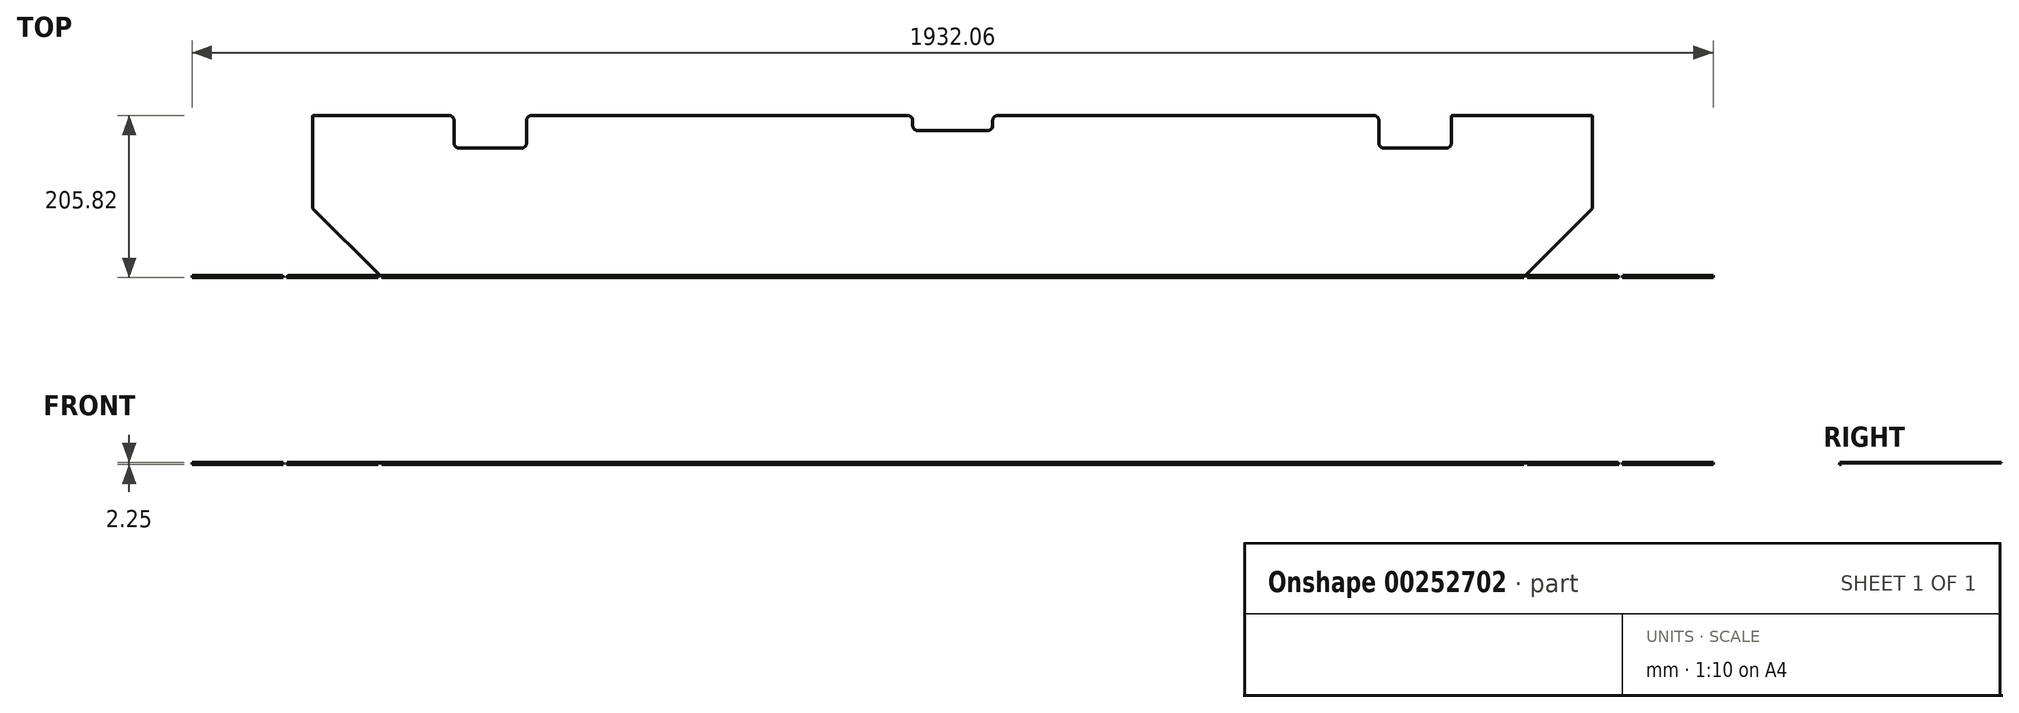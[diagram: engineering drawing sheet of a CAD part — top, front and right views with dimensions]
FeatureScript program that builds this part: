
annotation { "Feature Type Name" : "Feature", "Feature Type Description" : "" }
export const myFeature = defineFeature(function(context is Context, id is Id, definition is map)
    precondition{}
    {
        {
            assignVariable(context, id + "F0", {"name" : "Thickness", "anyValue" : .4});
        }
        {
            assignVariable(context, id + "F1", {"name" : "Height", "anyValue" : 2.25});
        }
        {
            var Q0;
            Q0=qCreatedBy(makeId("Top.planeOp"),FACE);
            var sketch = newSketch(context, id + "F2", { "sketchPlane" : qUnion([Q0])});
            skLineSegment(sketch, "E0.bottom", {"start": v(-812.8, 0) * mm, "end": v(812.8, 0) * mm});
            skLineSegment(sketch, "E0.top", {"start": v(-727.49, -203.2) * mm, "end": v(727.49, -203.2) * mm});
            skLineSegment(sketch, "E0.left", {"start": v(-812.8, 0) * mm, "end": v(-812.8, -117.89) * mm});
            skLineSegment(sketch, "E0.right", {"start": v(812.8, 0) * mm, "end": v(812.8, -117.89) * mm});
            skLineSegment(sketch, "E1", {"start": v(0, 0) * mm, "end": v(0, -68.91) * mm, "construction": true});
            skLineSegment(sketch, "E2", {"start": v(-812.8, -117.89) * mm, "end": v(-727.49, -203.2) * mm});
            skLineSegment(sketch, "E3", {"start": v(727.49, -203.2) * mm, "end": v(812.8, -117.89) * mm});
            skSolve(sketch);
        }
        {
            var Q0;
            Q0=qSketchRegion(id+"F2",true);
            extrude(context, id + "F3", {"entities" : qUnion([Q0]), "oppositeDirection" : true, "depth" : (getVariable(context, 'Thickness')) * mm});
        }
        {
            var Q0;
            Q0=makeQuery(id+"F3.opExtrude","CAP_FACE",FACE,{"disambiguationData":[OSD([sQuery(id+"F2.wireOp",EDGE,"E0.bottom"),sQuery(id+"F2.wireOp",EDGE,"E0.top"),sQuery(id+"F2.wireOp",EDGE,"E0.left"),sQuery(id+"F2.wireOp",EDGE,"E0.right"),sQuery(id+"F2.wireOp",EDGE,"E2"),sQuery(id+"F2.wireOp",EDGE,"E3")])],"isStart":true});
            var sketch = newSketch(context, id + "F4", { "sketchPlane" : qUnion([Q0])});
            skLineSegment(sketch, "E4.bottom", {"start": v(-1016, -203.2) * mm, "end": v(1016, -203.2) * mm});
            skLineSegment(sketch, "E4.top", {"start": v(-1016, -211.14) * mm, "end": v(1016, -211.14) * mm});
            skLineSegment(sketch, "E4.left", {"start": v(-1016, -203.2) * mm, "end": v(-1016, -211.14) * mm});
            skLineSegment(sketch, "E4.right", {"start": v(1016, -203.2) * mm, "end": v(1016, -211.14) * mm});
            skSolve(sketch);
        }
        {
            var Q0;
            Q0=qSketchRegion(id+"F4",true);
            extrude(context, id + "F5", {"entities" : qUnion([Q0]), "oppositeDirection" : true, "depth" : (getVariable(context, 'Height')) * mm});
        }
        {
            var Q0;
            Q0=qCreatedBy(makeId("Right.planeOp"),FACE);
            var sketch = newSketch(context, id + "F6", { "sketchPlane" : qUnion([Q0])});
            skLineSegment(sketch, "E5", {"start": v(-209.64, -12.7) * mm, "end": v(-211.14, -12.7) * mm});
            skLineSegment(sketch, "E6", {"start": v(-211.14, -12.7) * mm, "end": v(-211.14, 0) * mm});
            skLineSegment(sketch, "E7", {"start": v(-211.14, 0) * mm, "end": v(-204.7, 0) * mm});
            skFitSpline(sketch, "E8", {"points": [v(-204.7, 0) * mm, v(-204.89, -0.82) * mm, v(-207.45, -4.89) * mm, v(-209.64, -12.7) * mm], "startDerivative": vector(0, -4.3) * mm, "endDerivative": vector(-0.41, -10.99) * mm});
            skSolve(sketch);
        }
        {
            var Q0;
            Q0=qSketchRegion(id+"F6",true);
            extrude(context, id + "F7", {"entities" : qUnion([Q0]), "operationType" : NewBodyOperationType.REMOVE, "endBound" : BoundingType.THROUGH_ALL, "oppositeDirection" : true, "depth" : 25.4 * mm, "hasSecondDirection" : true, "secondDirectionBound" : SecondDirectionBoundingType.THROUGH_ALL, "secondDirectionOppositeDirection" : false, "secondDirectionDepth" : 25.4 * mm});
        }
        {
            var Q0;
            Q0=makeQuery(id+"F5.opExtrude","SWEPT_FACE",FACE,{"disambiguationData":[OSD([sQuery(id+"F4.wireOp",EDGE,"E4.right")])]});
            var sketch = newSketch(context, id + "F8", { "sketchPlane" : qUnion([Q0])});
            skLineSegment(sketch, "E9", {"start": v(-211.14, -31.75) * mm, "end": v(-211.14, -57.15) * mm});
            skLineSegment(sketch, "E10", {"start": v(-211.14, -57.15) * mm, "end": v(-203.2, -57.15) * mm});
            skLineSegment(sketch, "E11", {"start": v(-203.2, -57.15) * mm, "end": v(-203.2, -23.81) * mm});
            skLineSegment(sketch, "E12", {"start": v(-203.2, -23.81) * mm, "end": v(-211.14, -31.75) * mm});
            skSolve(sketch);
        }
        {
            var Q0;
            Q0 = qSketchRegion(id + "F8", true);
            extrude(context, id + "F9", {"entities" : qUnion([Q0]), "operationType" : NewBodyOperationType.REMOVE, "endBound" : BoundingType.THROUGH_ALL, "oppositeDirection" : true, "depth" : 25.4 * mm});
        }
        {
            var Q0;
            Q0=makeQuery(id+"F5.opExtrude","CAP_FACE",FACE,{"disambiguationData":[OSD([sQuery(id+"F4.wireOp",EDGE,"E4.bottom"),sQuery(id+"F4.wireOp",EDGE,"E4.top"),sQuery(id+"F4.wireOp",EDGE,"E4.left"),sQuery(id+"F4.wireOp",EDGE,"E4.right")])],"isStart":true});
            var sketch = newSketch(context, id + "F10", { "sketchPlane" : qUnion([Q0])});
            skLineSegment(sketch, "E13", {"start": v(-724.2, -203.2) * mm, "end": v(-727.49, -211.14) * mm});
            skLineSegment(sketch, "E14", {"start": v(-727.49, -211.14) * mm, "end": v(-730.78, -203.2) * mm});
            skLineSegment(sketch, "E15", {"start": v(-730.78, -203.2) * mm, "end": v(-724.2, -203.2) * mm});
            skLineSegment(sketch, "E16", {"start": v(-727.49, -211.14) * mm, "end": v(-727.49, -203.2) * mm, "construction": true});
            skPoint(sketch, "E16.endSnap0", {"position": v(-727.49, -203.2) * mm});
            skLineSegment(sketch, "E17", {"start": v(-844.85, -203.2) * mm, "end": v(-848.14, -211.14) * mm});
            skLineSegment(sketch, "E18", {"start": v(-848.14, -211.14) * mm, "end": v(-851.43, -203.2) * mm});
            skLineSegment(sketch, "E19", {"start": v(-851.43, -203.2) * mm, "end": v(-844.85, -203.2) * mm});
            skLineSegment(sketch, "E20", {"start": v(-848.14, -211.14) * mm, "end": v(-848.14, -203.2) * mm, "construction": true});
            skPoint(sketch, "E20.endSnap0", {"position": v(-848.14, -203.2) * mm});
            skLineSegment(sketch, "E21", {"start": v(0, 0) * mm, "end": v(0, -289.87) * mm, "construction": true});
            skLineSegment(sketch, "E22.MirrorCS", {"start": v(724.2, -203.2) * mm, "end": v(727.49, -211.14) * mm});
            skLineSegment(sketch, "E23.MirrorCS", {"start": v(727.49, -211.14) * mm, "end": v(730.78, -203.2) * mm});
            skLineSegment(sketch, "E24.MirrorCS", {"start": v(727.49, -211.14) * mm, "end": v(727.49, -203.2) * mm, "construction": true});
            skLineSegment(sketch, "E25.MirrorCS", {"start": v(730.78, -203.2) * mm, "end": v(724.2, -203.2) * mm});
            skLineSegment(sketch, "E26.MirrorCS", {"start": v(844.85, -203.2) * mm, "end": v(848.14, -211.14) * mm});
            skLineSegment(sketch, "E27.MirrorCS", {"start": v(848.14, -211.14) * mm, "end": v(851.43, -203.2) * mm});
            skLineSegment(sketch, "E28.MirrorCS", {"start": v(851.43, -203.2) * mm, "end": v(844.85, -203.2) * mm});
            skLineSegment(sketch, "E29.MirrorCS", {"start": v(848.14, -211.14) * mm, "end": v(848.14, -203.2) * mm, "construction": true});
            skPoint(sketch, "E30.MirrorP", {"position": v(727.49, -203.2) * mm});
            skPoint(sketch, "E31.MirrorP", {"position": v(848.14, -203.2) * mm});
            skLineSegment(sketch, "E32.bottom", {"start": v(-1016, -203.2) * mm, "end": v(-966.03, -203.2) * mm});
            skLineSegment(sketch, "E32.top", {"start": v(-1016, -211.14) * mm, "end": v(-966.03, -211.14) * mm});
            skLineSegment(sketch, "E32.left", {"start": v(-1016, -203.2) * mm, "end": v(-1016, -211.14) * mm});
            skLineSegment(sketch, "E32.right", {"start": v(-966.03, -203.2) * mm, "end": v(-966.03, -211.14) * mm});
            skLineSegment(sketch, "E33.MirrorCS", {"start": v(1016, -203.2) * mm, "end": v(1016, -211.14) * mm});
            skLineSegment(sketch, "E34.MirrorCS", {"start": v(966.03, -203.2) * mm, "end": v(966.03, -211.14) * mm});
            skLineSegment(sketch, "E35.MirrorCS", {"start": v(1016, -211.14) * mm, "end": v(966.03, -211.14) * mm});
            skLineSegment(sketch, "E36.MirrorCS", {"start": v(1016, -203.2) * mm, "end": v(966.03, -203.2) * mm});
            skLineSegment(sketch, "E37.0", {"start": v(-812.8, -117.89) * mm, "end": v(-727.49, -203.2) * mm, "construction": true});
            skLineSegment(sketch, "E38", {"start": v(-848.14, -211.14) * mm, "end": v(-727.49, -211.14) * mm, "construction": true});
            skLineSegment(sketch, "E39", {"start": v(-812.8, -117.89) * mm, "end": v(-812.8, 0) * mm, "construction": true});
            skLineSegment(sketch, "E40", {"start": v(-966.03, -211.14) * mm, "end": v(-848.14, -211.14) * mm, "construction": true});
            skSolve(sketch);
        }
        {
            var Q0;
            Q0=qSketchRegion(id+"F10",true);
            extrude(context, id + "F11", {"entities" : qUnion([Q0]), "operationType" : NewBodyOperationType.REMOVE, "endBound" : BoundingType.THROUGH_ALL, "oppositeDirection" : true, "depth" : 25.4 * mm});
        }
        {
            var Q0;
            Q0=makeQuery(id+"F3.opExtrude","CAP_FACE",FACE,{"disambiguationData":[OSD([sQuery(id+"F2.wireOp",EDGE,"E0.bottom"),sQuery(id+"F2.wireOp",EDGE,"E0.top"),sQuery(id+"F2.wireOp",EDGE,"E0.left"),sQuery(id+"F2.wireOp",EDGE,"E0.right"),sQuery(id+"F2.wireOp",EDGE,"E2"),sQuery(id+"F2.wireOp",EDGE,"E3")])],"isStart":true});
            var sketch = newSketch(context, id + "F12", { "sketchPlane" : qUnion([Q0])});
            skLineSegment(sketch, "E41", {"start": v(0, 0) * mm, "end": v(0, -203.2) * mm, "construction": true});
            skLineSegment(sketch, "E42.bottom", {"start": v(-633.41, 0) * mm, "end": v(-541.34, 0) * mm});
            skLineSegment(sketch, "E42.top", {"start": v(-633.41, -41.28) * mm, "end": v(-541.34, -41.28) * mm});
            skLineSegment(sketch, "E42.left", {"start": v(-541.34, 0) * mm, "end": v(-541.34, -41.27) * mm});
            skLineSegment(sketch, "E42.right", {"start": v(-633.41, 0) * mm, "end": v(-633.41, -41.27) * mm});
            skLineSegment(sketch, "E43.bottom", {"start": v(-50.8, 0) * mm, "end": v(50.8, 0) * mm});
            skLineSegment(sketch, "E43.top", {"start": v(-50.8, -19.05) * mm, "end": v(50.8, -19.05) * mm});
            skLineSegment(sketch, "E43.left", {"start": v(-50.8, 0) * mm, "end": v(-50.8, -19.05) * mm});
            skLineSegment(sketch, "E43.right", {"start": v(50.8, 0) * mm, "end": v(50.8, -19.05) * mm});
            skLineSegment(sketch, "E44.MirrorCS", {"start": v(633.41, 0) * mm, "end": v(633.41, -41.27) * mm});
            skLineSegment(sketch, "E45.MirrorCS", {"start": v(633.41, -41.28) * mm, "end": v(541.34, -41.28) * mm});
            skLineSegment(sketch, "E46.MirrorCS", {"start": v(633.41, 0) * mm, "end": v(541.34, 0) * mm});
            skLineSegment(sketch, "E47.MirrorCS", {"start": v(541.34, 0) * mm, "end": v(541.34, -41.27) * mm});
            skLineSegment(sketch, "E48", {"start": v(-587.38, -146.35) * mm, "end": v(-587.38, -41.27) * mm, "construction": true});
            skSolve(sketch);
        }
        {
            var Q0;
            Q0=qSketchRegion(id+"F12",true);
            extrude(context, id + "F13", {"entities" : qUnion([Q0]), "operationType" : NewBodyOperationType.REMOVE, "endBound" : BoundingType.THROUGH_ALL, "oppositeDirection" : true, "depth" : 25.4 * mm});
        }
        {
            var Q0;
            Q0=makeQuery(id+"F13.boolean.opBoolean","COPY",EDGE,{"derivedFrom":makeQuery(id+"F13.opExtrude","SWEPT_EDGE",EDGE,{"disambiguationData":[OSD([sQuery(id+"F2.wireOp",EDGE,"E0.bottom"),sQuery(id+"F12.wireOp",EDGE,"E42.bottom"),sQuery(id+"F12.wireOp",EDGE,"E42.right")])]})});
            var Q1;
            Q1=makeQuery(id+"F13.boolean.opBoolean","COPY",EDGE,{"derivedFrom":makeQuery(id+"F13.opExtrude","SWEPT_EDGE",EDGE,{"disambiguationData":[OSD([sQuery(id+"F12.wireOp",EDGE,"E42.top"),sQuery(id+"F12.wireOp",EDGE,"E42.right")])]})});
            var Q2;
            Q2=makeQuery(id+"F13.boolean.opBoolean","COPY",EDGE,{"derivedFrom":makeQuery(id+"F13.opExtrude","SWEPT_EDGE",EDGE,{"disambiguationData":[OSD([sQuery(id+"F12.wireOp",EDGE,"E42.top"),sQuery(id+"F12.wireOp",EDGE,"E42.left")])]})});
            var Q3;
            Q3=makeQuery(id+"F13.boolean.opBoolean","COPY",EDGE,{"derivedFrom":makeQuery(id+"F13.opExtrude","SWEPT_EDGE",EDGE,{"disambiguationData":[OSD([sQuery(id+"F2.wireOp",EDGE,"E0.bottom"),sQuery(id+"F12.wireOp",EDGE,"E42.bottom"),sQuery(id+"F12.wireOp",EDGE,"E42.left")])]})});
            var Q4;
            Q4=makeQuery(id+"F13.boolean.opBoolean","COPY",EDGE,{"derivedFrom":makeQuery(id+"F13.opExtrude","SWEPT_EDGE",EDGE,{"disambiguationData":[OSD([sQuery(id+"F12.wireOp",EDGE,"E43.top"),sQuery(id+"F12.wireOp",EDGE,"E43.left")])]})});
            var Q5;
            Q5=makeQuery(id+"F13.boolean.opBoolean","COPY",EDGE,{"derivedFrom":makeQuery(id+"F13.opExtrude","SWEPT_EDGE",EDGE,{"disambiguationData":[OSD([sQuery(id+"F2.wireOp",EDGE,"E0.bottom"),sQuery(id+"F12.wireOp",EDGE,"E43.bottom"),sQuery(id+"F12.wireOp",EDGE,"E43.left")])]})});
            var Q6;
            Q6=makeQuery(id+"F13.boolean.opBoolean","COPY",EDGE,{"derivedFrom":makeQuery(id+"F13.opExtrude","SWEPT_EDGE",EDGE,{"disambiguationData":[OSD([sQuery(id+"F2.wireOp",EDGE,"E0.bottom"),sQuery(id+"F12.wireOp",EDGE,"E43.bottom"),sQuery(id+"F12.wireOp",EDGE,"E43.right")])]})});
            var Q7;
            Q7=makeQuery(id+"F13.boolean.opBoolean","COPY",EDGE,{"derivedFrom":makeQuery(id+"F13.opExtrude","SWEPT_EDGE",EDGE,{"disambiguationData":[OSD([sQuery(id+"F12.wireOp",EDGE,"E43.top"),sQuery(id+"F12.wireOp",EDGE,"E43.right")])]})});
            var Q8;
            Q8=makeQuery(id+"F13.boolean.opBoolean","COPY",EDGE,{"derivedFrom":makeQuery(id+"F13.opExtrude","SWEPT_EDGE",EDGE,{"disambiguationData":[OSD([sQuery(id+"F12.wireOp",EDGE,"E44.MirrorCS"),sQuery(id+"F12.wireOp",EDGE,"E45.MirrorCS")])]})});
            var Q9;
            Q9=makeQuery(id+"F13.boolean.opBoolean","COPY",EDGE,{"derivedFrom":makeQuery(id+"F13.opExtrude","SWEPT_EDGE",EDGE,{"disambiguationData":[OSD([sQuery(id+"F2.wireOp",EDGE,"E0.bottom"),sQuery(id+"F12.wireOp",EDGE,"E44.MirrorCS"),sQuery(id+"F12.wireOp",EDGE,"E46.MirrorCS")])]})});
            var Q10;
            Q10=makeQuery(id+"F13.boolean.opBoolean","COPY",EDGE,{"derivedFrom":makeQuery(id+"F13.opExtrude","SWEPT_EDGE",EDGE,{"disambiguationData":[OSD([sQuery(id+"F12.wireOp",EDGE,"E45.MirrorCS"),sQuery(id+"F12.wireOp",EDGE,"E47.MirrorCS")])]})});
            var Q11;
            Q11=makeQuery(id+"F13.boolean.opBoolean","COPY",EDGE,{"derivedFrom":makeQuery(id+"F13.opExtrude","SWEPT_EDGE",EDGE,{"disambiguationData":[OSD([sQuery(id+"F2.wireOp",EDGE,"E0.bottom"),sQuery(id+"F12.wireOp",EDGE,"E46.MirrorCS"),sQuery(id+"F12.wireOp",EDGE,"E47.MirrorCS")])]})});
            fillet(context, id + "F14", {"entities" : qUnion([Q0, Q1, Q2, Q3, Q4, Q5, Q6, Q7, Q8, Q9, Q10, Q11]), "radius" : 6.35 * mm, "tangentPropagation" : true, "allowEdgeOverflow" : false});
        }
        {
            var Q0;
            Q0=makeQuery(id+"F3.opExtrude","CAP_EDGE",EDGE,{"disambiguationData":[OSD([sQuery(id+"F2.wireOp",EDGE,"E3")])],"isStart":false});
            var Q1;
            Q1=makeQuery(id+"F3.opExtrude","CAP_EDGE",EDGE,{"disambiguationData":[OSD([sQuery(id+"F2.wireOp",EDGE,"E0.right")])],"isStart":false});
            var Q2;
            Q2=makeQuery(id+"F3.opExtrude","CAP_EDGE",EDGE,{"disambiguationData":[OSD([sQuery(id+"F2.wireOp",EDGE,"E0.left")])],"isStart":false});
            var Q3;
            Q3=makeQuery(id+"F3.opExtrude","CAP_EDGE",EDGE,{"disambiguationData":[OSD([sQuery(id+"F2.wireOp",EDGE,"E2")])],"isStart":false});
            var Q4;
            Q4=makeQuery(id+"F3.opExtrude","CAP_EDGE",EDGE,{"disambiguationData":[OSD([sQuery(id+"F2.wireOp",EDGE,"E0.top")])],"isStart":false});
            chamfer(context, id + "F15", {"entities" : qUnion([Q0, Q1, Q2, Q3, Q4]), "width" : (getVariable(context, 'Thickness')) * mm, "tangentPropagation" : true});
        }
    });
